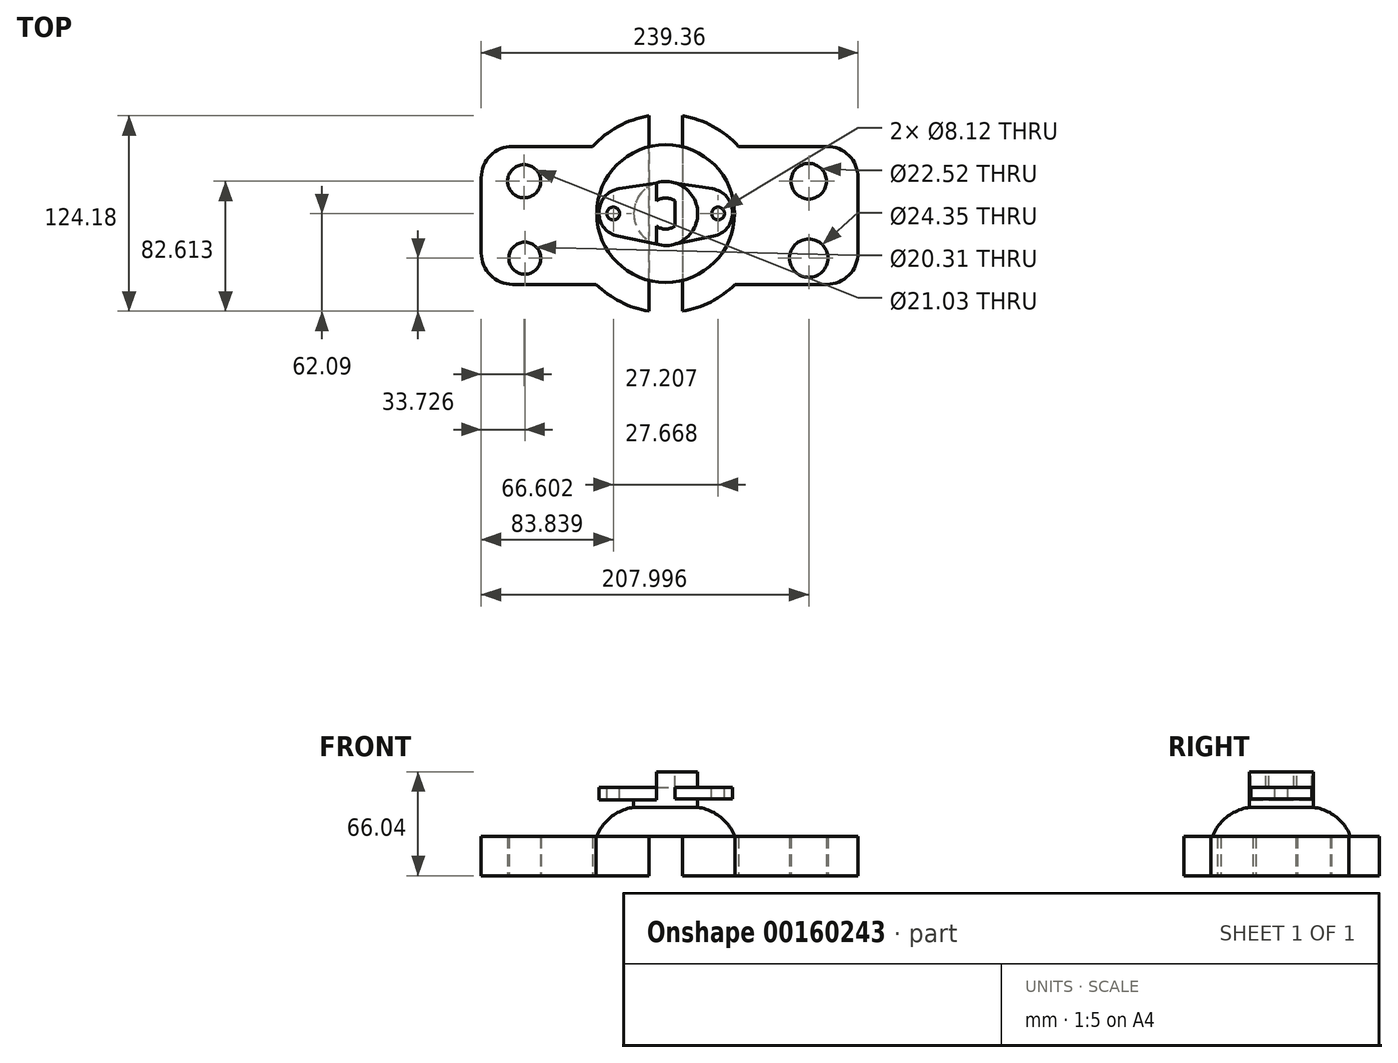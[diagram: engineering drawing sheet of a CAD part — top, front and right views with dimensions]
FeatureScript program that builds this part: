
annotation { "Feature Type Name" : "Feature", "Feature Type Description" : "" }
export const myFeature = defineFeature(function(context is Context, id is Id, definition is map)
    precondition{}
    {
        {
            var Q0;
            Q0=qCreatedBy(makeId("Top.planeOp"),FACE);
            var sketch = newSketch(context, id + "F0", { "sketchPlane" : qUnion([Q0])});
            skLineSegment(sketch, "E0.bottom", {"start": v(-117.14, 42.66) * mm, "end": v(122.22, 42.66) * mm});
            skLineSegment(sketch, "E0.top", {"start": v(-117.14, -44.97) * mm, "end": v(122.22, -44.97) * mm});
            skLineSegment(sketch, "E0.left", {"start": v(-117.14, 42.66) * mm, "end": v(-117.14, -44.97) * mm});
            skLineSegment(sketch, "E0.right", {"start": v(122.22, 42.66) * mm, "end": v(122.22, -44.97) * mm});
            skCircle(sketch, "E1", {"center": v(-89.93, 20.52) * mm, "radius": 10.52 * mm});
            skCircle(sketch, "E2", {"center": v(90.86, 20.52) * mm, "radius": 11.26 * mm});
            skCircle(sketch, "E3", {"center": v(90.86, -28.36) * mm, "radius": 12.18 * mm});
            skCircle(sketch, "E4", {"center": v(-89.47, -28.36) * mm, "radius": 10.16 * mm});
            skCircle(sketch, "E5", {"center": v(0, 0) * mm, "radius": 63 * mm});
            skLineSegment(sketch, "E6.bottom", {"start": v(-10.73, 68.53) * mm, "end": v(10.68, 68.53) * mm});
            skLineSegment(sketch, "E6.top", {"start": v(-10.73, -71.33) * mm, "end": v(10.68, -71.33) * mm});
            skLineSegment(sketch, "E6.left", {"start": v(-10.73, 68.53) * mm, "end": v(-10.73, -71.33) * mm});
            skLineSegment(sketch, "E6.right", {"start": v(10.68, 68.53) * mm, "end": v(10.68, -71.33) * mm});
            skSolve(sketch);
        }
        {
            var Q0;
            Q0 = qSketchRegion(id + "F0", true);
            extrude(context, id + "F1", {"entities" : qUnion([Q0]), "depth" : 25 * mm});
        }
        {
            var Q0;
            Q0=makeQuery(id+"F1.opExtrude","SWEPT_EDGE",EDGE,{"disambiguationData":[OSD([sQuery(id+"F0.wireOp",EDGE,"E0.top"),sQuery(id+"F0.wireOp",EDGE,"E0.left")])]});
            fillet(context, id + "F2", {"entities" : qUnion([Q0]), "radius" : 20 * mm, "tangentPropagation" : true, "allowEdgeOverflow" : false});
        }
        {
            var Q0;
            Q0=makeQuery(id+"F1.opExtrude","SWEPT_EDGE",EDGE,{"disambiguationData":[OSD([sQuery(id+"F0.wireOp",EDGE,"E0.bottom"),sQuery(id+"F0.wireOp",EDGE,"E0.left")])]});
            fillet(context, id + "F3", {"entities" : qUnion([Q0]), "radius" : 20 * mm, "tangentPropagation" : true, "allowEdgeOverflow" : false});
        }
        {
            var Q0;
            Q0=makeQuery(id+"F1.opExtrude","SWEPT_EDGE",EDGE,{"disambiguationData":[OSD([sQuery(id+"F0.wireOp",EDGE,"E0.bottom"),sQuery(id+"F0.wireOp",EDGE,"E0.right")])]});
            fillet(context, id + "F4", {"entities" : qUnion([Q0]), "radius" : 20 * mm, "tangentPropagation" : true, "allowEdgeOverflow" : false});
        }
        {
            var Q0;
            Q0=makeQuery(id+"F1.opExtrude","SWEPT_EDGE",EDGE,{"disambiguationData":[OSD([sQuery(id+"F0.wireOp",EDGE,"E0.top"),sQuery(id+"F0.wireOp",EDGE,"E0.right")])]});
            fillet(context, id + "F5", {"entities" : qUnion([Q0]), "radius" : 20 * mm, "tangentPropagation" : true, "allowEdgeOverflow" : false});
        }
        {
            var Q0;
            {var subQ5=sQuery(id+"F0.wireOp",EDGE,"E6.bottom");Q0=makeQuery(id+"F0.imprint","IMPRINT",FACE,{"disambiguationData":[TD([[makeQuery(id+"F0.imprint","IMPRINT",EDGE,{"derivedFrom":subQ5}),-1.0]])]});}
            extrude(context, id + "F6", {"entities" : qUnion([Q0]), "operationType" : NewBodyOperationType.REMOVE, "depth" : 84.25 * mm});
        }
        {
            var Q0;
            {var subQ0=sQuery(id+"F0.wireOp",EDGE,"E6.left");var subQ1=sQuery(id+"F0.wireOp",EDGE,"E0.bottom");var subQ2=makeQuery(id+"F0.imprint","INTERSECT",VERTEX,{"derivedFrom":[subQ1,subQ0]});Q0=makeQuery(id+"F0.imprint","IMPRINT",FACE,{"disambiguationData":[TD([[makeQuery(id+"F0.imprint","IMPRINT",EDGE,{"disambiguationData":[TD([[subQ2,-1.0]])],"derivedFrom":subQ1}),1.0]])]});}
            extrude(context, id + "F7", {"entities" : qUnion([Q0]), "operationType" : NewBodyOperationType.REMOVE, "depth" : 100 * mm});
        }
        {
            var Q0;
            {var subQ0=sQuery(id+"F0.wireOp",EDGE,"E6.left");var subQ1=sQuery(id+"F0.wireOp",EDGE,"E0.top");var subQ2=makeQuery(id+"F0.imprint","INTERSECT",VERTEX,{"derivedFrom":[subQ1,subQ0]});Q0=makeQuery(id+"F0.imprint","IMPRINT",FACE,{"disambiguationData":[TD([[makeQuery(id+"F0.imprint","IMPRINT",EDGE,{"disambiguationData":[TD([[subQ2,-1.0]])],"derivedFrom":subQ1}),-1.0]])]});}
            extrude(context, id + "F8", {"entities" : qUnion([Q0]), "operationType" : NewBodyOperationType.REMOVE, "depth" : 95.25 * mm});
        }
        {
            var Q0;
            {var subQ5=sQuery(id+"F0.wireOp",EDGE,"E6.top");Q0=makeQuery(id+"F0.imprint","IMPRINT",FACE,{"disambiguationData":[TD([[makeQuery(id+"F0.imprint","IMPRINT",EDGE,{"derivedFrom":subQ5}),1.0]])]});}
            extrude(context, id + "F9", {"entities" : qUnion([Q0]), "operationType" : NewBodyOperationType.REMOVE, "depth" : 74.75 * mm});
        }
        {
            var Q0;
            Q0=qCreatedBy(makeId("Right.planeOp"),FACE);
            var sketch = newSketch(context, id + "F10", { "sketchPlane" : qUnion([Q0])});
            skLineSegment(sketch, "E7", {"start": v(0, 25.16) * mm, "end": v(0, 66.04) * mm});
            skLineSegment(sketch, "E8", {"start": v(-20.32, 25.14) * mm, "end": v(0, 25.16) * mm});
            skLineSegment(sketch, "E9", {"start": v(-20.32, 25.14) * mm, "end": v(-43.76, 25.11) * mm});
            skLineSegment(sketch, "E10", {"start": v(-20.32, 25.14) * mm, "end": v(-20.32, 66.04) * mm});
            skLineSegment(sketch, "E11", {"start": v(-20.32, 66.04) * mm, "end": v(0, 66.04) * mm});
            skArc(sketch, "E12", {"start": v(-20.32, 43.44) * mm, "mid": v(-34.54, 37.47) * mm, "end": v(-43.76, 25.11) * mm});
            skSolve(sketch);
        }
        {
            var Q0;
            Q0=makeQuery(id+"F10.imprint","IMPRINT",FACE,{"disambiguationData":[TD([[makeQuery(id+"F10.imprint","IMPRINT",EDGE,{"derivedFrom":sQuery(id+"F10.wireOp",EDGE,"E7")}),1.0]])]});
            var Q1;
            Q1=sQuery(id+"F10.wireOp",EDGE,"E7");
            revolve(context, id + "F11", {"entities" : qUnion([Q0]), "axis" : qUnion([Q1]), "revolveType" : RevolveType.FULL});
        }
        {
            var Q0;
            Q0 = qSketchRegion(id + "F10", true);
            var Q1;
            Q1=makeQuery(id+"F11.opRevolve","SWEPT_FACE",FACE,{"disambiguationData":[OSD([sQuery(id+"F10.wireOp",EDGE,"E10")])]});
            revolve(context, id + "F12", {"operationType" : NewBodyOperationType.ADD, "entities" : qUnion([Q0]), "axis" : qUnion([Q1]), "revolveType" : RevolveType.FULL});
        }
        {
            var Q0;
            Q0=makeQuery(id+"F11.opRevolve","SWEPT_FACE",FACE,{"disambiguationData":[OSD([sQuery(id+"F10.wireOp",EDGE,"E11")])]});
            var sketch = newSketch(context, id + "F13", { "sketchPlane" : qUnion([Q0])});
            skCircle(sketch, "E13", {"center": v(0, 0) * mm, "radius": 9.86 * mm});
            skLineSegment(sketch, "E14.bottom", {"start": v(-5.84, 23.39) * mm, "end": v(5.8, 23.39) * mm});
            skLineSegment(sketch, "E14.top", {"start": v(-5.84, -24.32) * mm, "end": v(5.8, -24.32) * mm});
            skLineSegment(sketch, "E14.left", {"start": v(-5.84, 23.39) * mm, "end": v(-5.84, -24.32) * mm});
            skLineSegment(sketch, "E14.right", {"start": v(5.8, 23.39) * mm, "end": v(5.8, -24.32) * mm});
            skSolve(sketch);
        }
        {
            var Q0;
            {var subQ0=sQuery(id+"F13.wireOp",EDGE,"E14.left");var subQ1=sQuery(id+"F13.wireOp",EDGE,"E13");var subQ2=makeQuery(id+"F13.imprint","INTERSECT",VERTEX,{"disambiguationData":[OD(0.0)],"derivedFrom":[subQ1,subQ0]});Q0=makeQuery(id+"F13.imprint","IMPRINT",FACE,{"disambiguationData":[TD([[makeQuery(id+"F13.imprint","IMPRINT",EDGE,{"disambiguationData":[TD([[subQ2,1.0]])],"derivedFrom":subQ1}),1.0]])]});}
            extrude(context, id + "F14", {"entities" : qUnion([Q0]), "operationType" : NewBodyOperationType.REMOVE, "oppositeDirection" : true, "depth" : 10 * mm});
        }
        {
            var Q0;
            {var subQ0=sQuery(id+"F13.wireOp",EDGE,"E14.left");var subQ1=sQuery(id+"F13.wireOp",EDGE,"E13");var subQ2=makeQuery(id+"F13.imprint","INTERSECT",VERTEX,{"disambiguationData":[OD(0.0)],"derivedFrom":[subQ1,subQ0]});Q0=makeQuery(id+"F13.imprint","IMPRINT",FACE,{"disambiguationData":[TD([[makeQuery(id+"F13.imprint","IMPRINT",EDGE,{"disambiguationData":[TD([[subQ2,1.0]])],"derivedFrom":subQ1}),-1.0]])]});}
            extrude(context, id + "F15", {"entities" : qUnion([Q0]), "operationType" : NewBodyOperationType.REMOVE, "oppositeDirection" : true, "depth" : 10 * mm});
        }
        {
            var Q0;
            {var subQ0=sQuery(id+"F13.wireOp",EDGE,"E14.left");var subQ1=sQuery(id+"F13.wireOp",EDGE,"E13");var subQ2=makeQuery(id+"F13.imprint","INTERSECT",VERTEX,{"disambiguationData":[OD(1.0)],"derivedFrom":[subQ1,subQ0]});Q0=makeQuery(id+"F13.imprint","IMPRINT",FACE,{"disambiguationData":[TD([[makeQuery(id+"F13.imprint","IMPRINT",EDGE,{"disambiguationData":[TD([[subQ2,-1.0]])],"derivedFrom":subQ1}),-1.0]])]});}
            extrude(context, id + "F16", {"entities" : qUnion([Q0]), "operationType" : NewBodyOperationType.REMOVE, "oppositeDirection" : true, "depth" : 10 * mm});
        }
        {
            var Q0;
            {var subQ0=sQuery(id+"F13.wireOp",EDGE,"E14.left");var subQ1=sQuery(id+"F13.wireOp",EDGE,"E13");var subQ2=makeQuery(id+"F13.imprint","INTERSECT",VERTEX,{"disambiguationData":[OD(0.0)],"derivedFrom":[subQ1,subQ0]});Q0=makeQuery(id+"F13.imprint","IMPRINT",FACE,{"disambiguationData":[TD([[makeQuery(id+"F13.imprint","IMPRINT",EDGE,{"disambiguationData":[TD([[subQ2,-1.0]])],"derivedFrom":subQ1}),1.0]])]});}
            extrude(context, id + "F17", {"entities" : qUnion([Q0]), "operationType" : NewBodyOperationType.REMOVE, "oppositeDirection" : true, "depth" : 10 * mm});
        }
        {
            var Q0;
            {var subQ0=sQuery(id+"F13.wireOp",EDGE,"E14.right");var subQ1=sQuery(id+"F13.wireOp",EDGE,"E13");var subQ2=makeQuery(id+"F13.imprint","INTERSECT",VERTEX,{"disambiguationData":[OD(0.0)],"derivedFrom":[subQ1,subQ0]});Q0=makeQuery(id+"F13.imprint","IMPRINT",FACE,{"disambiguationData":[TD([[makeQuery(id+"F13.imprint","IMPRINT",EDGE,{"disambiguationData":[TD([[subQ2,1.0]])],"derivedFrom":subQ1}),1.0]])]});}
            extrude(context, id + "F18", {"entities" : qUnion([Q0]), "operationType" : NewBodyOperationType.REMOVE, "oppositeDirection" : true, "depth" : 10 * mm});
        }
        {
            var Q0;
            {var subQ0=sQuery(id+"F13.wireOp",EDGE,"E14.right");var subQ1=sQuery(id+"F13.wireOp",EDGE,"E13");var subQ2=sQuery(id+"F13.wireOp",EDGE,"E14.left");var subQ3=sQuery(id+"F10.wireOp",EDGE,"E11");var subQ4=sQuery(id+"F10.wireOp",EDGE,"E10");Q0=makeQuery(id+"F18.boolean.opBoolean","MERGE",FACE,{"derivedFrom":[makeQuery(id+"F17.boolean.opBoolean","MERGE",FACE,{"derivedFrom":[makeQuery(id+"F16.boolean.opBoolean","MERGE",FACE,{"derivedFrom":[makeQuery(id+"F15.boolean.opBoolean","MERGE",FACE,{"derivedFrom":[makeQuery(id+"F14.boolean.opBoolean","COPY",FACE,{"derivedFrom":makeQuery(id+"F14.opExtrude","CAP_FACE",FACE,{"disambiguationData":[OSD([subQ1,subQ2,subQ0])],"isStart":false})}),makeQuery(id+"F15.opExtrude","CAP_FACE",FACE,{"disambiguationData":[OSD([subQ4,subQ3,subQ1,subQ2,subQ0])],"isStart":false})]}),makeQuery(id+"F16.opExtrude","CAP_FACE",FACE,{"disambiguationData":[OSD([subQ4,subQ3,subQ1,subQ2,subQ0])],"isStart":false})]}),makeQuery(id+"F17.opExtrude","CAP_FACE",FACE,{"disambiguationData":[OSD([subQ1,subQ2])],"isStart":false})]}),makeQuery(id+"F18.opExtrude","CAP_FACE",FACE,{"disambiguationData":[OSD([subQ1,subQ0])],"isStart":false})]});}
            var sketch = newSketch(context, id + "F19", { "sketchPlane" : qUnion([Q0])});
            skLineSegment(sketch, "E15", {"start": v(-5.84, 19.46) * mm, "end": v(-42.38, 13.7) * mm});
            skPoint(sketch, "E15.endSnap0", {"position": v(-5.84, 13.7) * mm});
            skLineSegment(sketch, "E16", {"start": v(-5.84, -19.46) * mm, "end": v(-42.38, -12.03) * mm});
            skLineSegment(sketch, "E17", {"start": v(-42.38, -12.03) * mm, "end": v(-42.38, 13.7) * mm});
            skLineSegment(sketch, "E18.MirrorCS", {"start": v(5.84, 19.46) * mm, "end": v(42.38, 13.7) * mm});
            skLineSegment(sketch, "E19.MirrorCS", {"start": v(5.84, -19.46) * mm, "end": v(42.38, -12.03) * mm});
            skLineSegment(sketch, "E20.MirrorCS", {"start": v(42.38, -12.03) * mm, "end": v(42.38, 13.7) * mm});
            skLineSegment(sketch, "E21", {"start": v(5.84, 19.46) * mm, "end": v(5.8, 7.97) * mm});
            skLineSegment(sketch, "E22", {"start": v(5.84, -19.46) * mm, "end": v(5.8, -7.97) * mm});
            skArc(sketch, "E23", {"start": v(5.8, -7.97) * mm, "mid": v(10.6, 0) * mm, "end": v(5.8, 7.97) * mm});
            skCircle(sketch, "E24", {"center": v(-33.3, 0) * mm, "radius": 4.06 * mm});
            skCircle(sketch, "E25.MirrorC", {"center": v(33.3, 0) * mm, "radius": 4.06 * mm});
            skSolve(sketch);
        }
        {
            var Q0;
            Q0=makeQuery(id+"F19.imprint","IMPRINT",FACE,{"disambiguationData":[TD([[makeQuery(id+"F19.imprint","IMPRINT",EDGE,{"derivedFrom":sQuery(id+"F19.wireOp",EDGE,"E15")}),1.0]])]});
            extrude(context, id + "F20", {"entities" : qUnion([Q0]), "operationType" : NewBodyOperationType.ADD, "oppositeDirection" : true, "depth" : 7.75 * mm});
        }
        {
            var Q0;
            Q0=makeQuery(id+"F20.opExtrude","SWEPT_EDGE",EDGE,{"disambiguationData":[OSD([sQuery(id+"F19.wireOp",EDGE,"E16"),sQuery(id+"F19.wireOp",EDGE,"E17")])]});
            fillet(context, id + "F21", {"entities" : qUnion([Q0]), "radius" : 15 * mm, "tangentPropagation" : true, "allowEdgeOverflow" : false});
        }
        {
            var Q0;
            Q0=makeQuery(id+"F20.opExtrude","SWEPT_EDGE",EDGE,{"disambiguationData":[OSD([sQuery(id+"F19.wireOp",EDGE,"E15"),sQuery(id+"F19.wireOp",EDGE,"E17")])]});
            fillet(context, id + "F22", {"entities" : qUnion([Q0]), "radius" : 15 * mm, "tangentPropagation" : true, "allowEdgeOverflow" : false});
        }
        {
            var Q0;
            Q0=makeQuery(id+"F19.imprint","IMPRINT",FACE,{"disambiguationData":[TD([[makeQuery(id+"F19.imprint","IMPRINT",EDGE,{"derivedFrom":sQuery(id+"F19.wireOp",EDGE,"E18.MirrorCS")}),-1.0]])]});
            extrude(context, id + "F23", {"entities" : qUnion([Q0]), "operationType" : NewBodyOperationType.ADD, "oppositeDirection" : true, "depth" : 7.25 * mm});
        }
        {
            var Q0;
            Q0=makeQuery(id+"F23.opExtrude","SWEPT_EDGE",EDGE,{"disambiguationData":[OSD([sQuery(id+"F19.wireOp",EDGE,"E18.MirrorCS"),sQuery(id+"F19.wireOp",EDGE,"E20.MirrorCS")])]});
            var Q1;
            Q1=makeQuery(id+"F23.opExtrude","SWEPT_EDGE",EDGE,{"disambiguationData":[OSD([sQuery(id+"F19.wireOp",EDGE,"E19.MirrorCS"),sQuery(id+"F19.wireOp",EDGE,"E20.MirrorCS")])]});
            fillet(context, id + "F24", {"entities" : qUnion([Q0, Q1]), "radius" : 15 * mm, "tangentPropagation" : true, "allowEdgeOverflow" : false});
        }
    });
